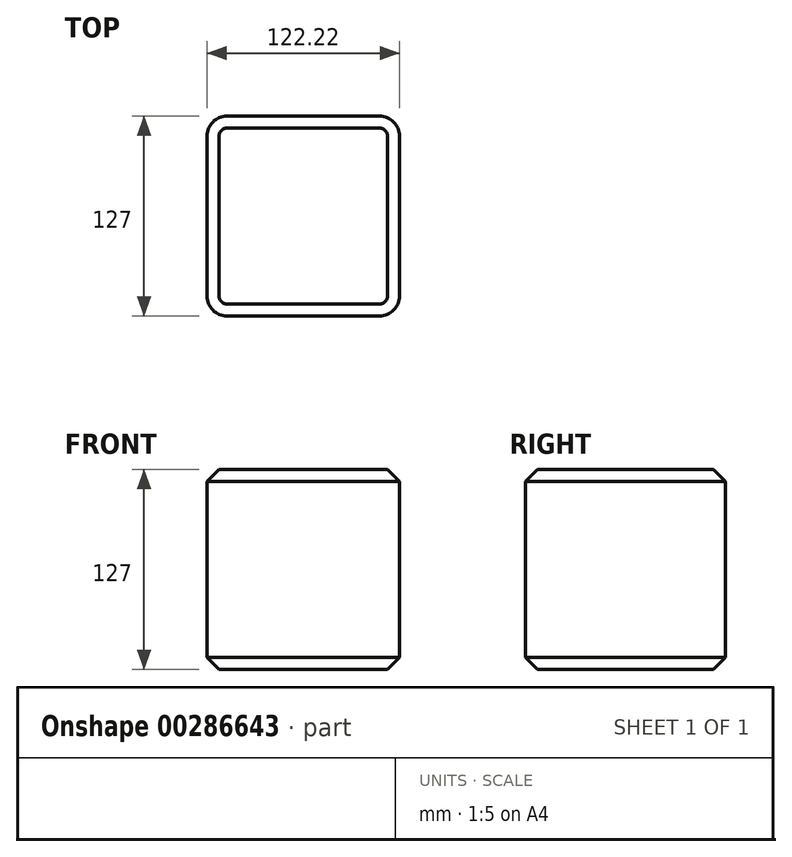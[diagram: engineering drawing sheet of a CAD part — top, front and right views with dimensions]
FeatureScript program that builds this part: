
annotation { "Feature Type Name" : "Feature", "Feature Type Description" : "" }
export const myFeature = defineFeature(function(context is Context, id is Id, definition is map)
    precondition{}
    {
        {
            var Q0;
            Q0=qCreatedBy(makeId("Top.planeOp"),FACE);
            var sketch = newSketch(context, id + "F0", { "sketchPlane" : qUnion([Q0])});
            skLineSegment(sketch, "E0.bottom", {"start": v(61.1, 63.5) * mm, "end": v(-61.1, 63.5) * mm});
            skLineSegment(sketch, "E0.top", {"start": v(61.1, -63.5) * mm, "end": v(-61.1, -63.5) * mm});
            skLineSegment(sketch, "E0.left", {"start": v(61.1, 63.5) * mm, "end": v(61.1, -63.5) * mm});
            skLineSegment(sketch, "E0.right", {"start": v(-61.1, 63.5) * mm, "end": v(-61.1, -63.5) * mm});
            skPoint(sketch, "E0.middle", {"position": v(0, 0) * mm});
            skSolve(sketch);
        }
        {
            var Q0;
            Q0 = qSketchRegion(id + "F0", true);
            extrude(context, id + "F1", {"entities" : qUnion([Q0]), "depth" : 127 * mm});
        }
        {
            var Q0;
            Q0=makeQuery(id+"F1.opExtrude","SWEPT_EDGE",EDGE,{"disambiguationData":[OSD([sQuery(id+"F0.wireOp",EDGE,"E0.bottom"),sQuery(id+"F0.wireOp",EDGE,"E0.left")])]});
            var Q1;
            Q1=makeQuery(id+"F1.opExtrude","SWEPT_EDGE",EDGE,{"disambiguationData":[OSD([sQuery(id+"F0.wireOp",EDGE,"E0.top"),sQuery(id+"F0.wireOp",EDGE,"E0.left")])]});
            var Q2;
            Q2=makeQuery(id+"F1.opExtrude","SWEPT_EDGE",EDGE,{"disambiguationData":[OSD([sQuery(id+"F0.wireOp",EDGE,"E0.top"),sQuery(id+"F0.wireOp",EDGE,"E0.right")])]});
            var Q3;
            Q3=makeQuery(id+"F1.opExtrude","SWEPT_EDGE",EDGE,{"disambiguationData":[OSD([sQuery(id+"F0.wireOp",EDGE,"E0.bottom"),sQuery(id+"F0.wireOp",EDGE,"E0.right")])]});
            fillet(context, id + "F2", {"entities" : qUnion([Q0, Q1, Q2, Q3]), "radius" : 12.7 * mm, "tangentPropagation" : true, "allowEdgeOverflow" : false});
        }
        {
            var Q0;
            Q0=makeQuery(id+"F1.opExtrude","CAP_EDGE",EDGE,{"disambiguationData":[OSD([sQuery(id+"F0.wireOp",EDGE,"E0.left")])],"isStart":false});
            var Q1;
            Q1=makeQuery(id+"F1.opExtrude","CAP_EDGE",EDGE,{"disambiguationData":[OSD([sQuery(id+"F0.wireOp",EDGE,"E0.left")])],"isStart":true});
            chamfer(context, id + "F3", {"entities" : qUnion([Q0, Q1]), "width" : 7.62 * mm, "tangentPropagation" : true});
        }
    });
